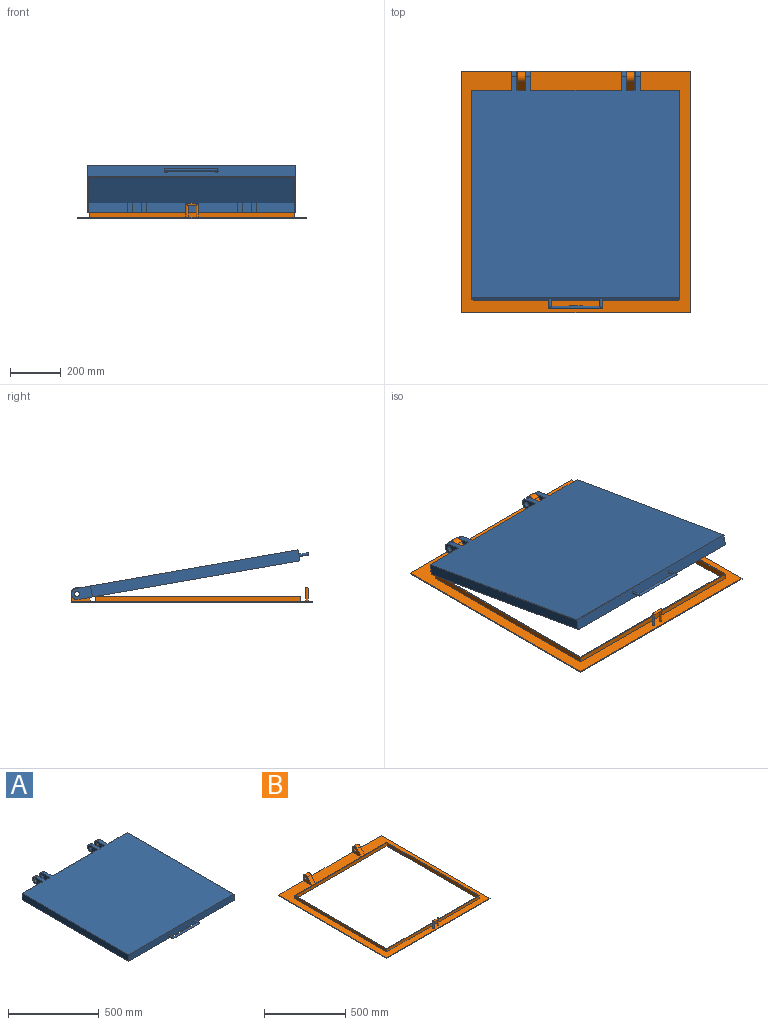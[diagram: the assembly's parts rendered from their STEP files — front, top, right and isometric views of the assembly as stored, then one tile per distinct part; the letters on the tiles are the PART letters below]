
ASSEMBLY  parts=2 mates=1
PART A: 38 faces, bbox 820x950x44 mm
  f0: plane 160x44mm, normal (0,1,0), area 7040mm2, adj f6,f8,f13,f25
  f1: plane 44x35mm, normal (0,1,0), area 1540mm2, adj f8,f13,f22,f24
  f2: plane 355x44mm, normal (0,1,0), area 15620mm2, adj f8,f13,f19,f23
  f3: plane 44x35mm, normal (0,1,0), area 1540mm2, adj f8,f13,f18,f21
  f4: plane 820x44mm, normal (0,-1,0), area 35922.9mm2, adj f6,f7,f8,f13,f15,f17
  f5: plane 155x44mm, normal (0,1,0), area 6820mm2, adj f7,f8,f13,f20
  f6: plane 830x44mm, normal (-1,0,0), area 36520mm2, adj f0,f4,f8,f13
  f7: plane 830x44mm, normal (1,0,0), area 36520mm2, adj f4,f5,f8,f13
  f8: plane 887.5x820mm, normal (0,0,1), area 685200mm2, adj f0,f1,f2,f3,f4,f5,f6,f7
  f9: plane 822x40mm, normal (-1,0,0), area 32880mm2, adj f10,f12,f13,f14
  f10: plane 812x40mm, normal (0,-1,0), area 32480mm2, adj f9,f11,f13,f14
  f11: plane 822x40mm, normal (1,0,0), area 32880mm2, adj f10,f12,f13,f14
  f12: plane 812x40mm, normal (0,1,0), area 32480mm2, adj f9,f11,f13,f14
  f13: plane 887.5x820mm, normal (0,0,-1), area 17736mm2, adj f0,f1,f2,f3,f4,f5,f6,f7
  f14: plane 822x812mm, normal (0,0,-1), area 667464mm2, adj f9,f10,f11,f12
  f15: cylinder r=5mm len=40mm, axis (0,1,0), area 1099.6mm2, adj f4,f16
  f16: cylinder r=5mm len=210mm, axis (1,0,0), area 6277.8mm2, adj f15,f17
  f17: cylinder r=5mm len=40mm, axis (0,-1,0), area 1094.2mm2, adj f4,f16
  f18: plane 79.99x44mm, normal (1,0,0), area 2988.6mm2, adj f3,f8,f13,f32,f33,f37
  f19: plane 79.99x44mm, normal (-1,0,0), area 2988.6mm2, adj f2,f8,f13,f32,f33,f37
  f20: plane 79.99x44mm, normal (1,0,0), area 2988.6mm2, adj f5,f8,f13,f30,f31,f36
  f21: plane 79.99x44mm, normal (-1,0,0), area 2988.6mm2, adj f3,f8,f13,f30,f31,f36
  f22: plane 79.99x44mm, normal (-1,0,0), area 2988.6mm2, adj f1,f8,f13,f28,f29,f35
  f23: plane 79.99x44mm, normal (1,0,0), area 2988.6mm2, adj f2,f8,f13,f28,f29,f35
  f24: plane 79.99x44mm, normal (1,0,0), area 2988.6mm2, adj f1,f8,f13,f26,f27,f34
  f25: plane 79.99x44mm, normal (-1,0,0), area 2988.6mm2, adj f0,f8,f13,f26,f27,f34
  f26: cylinder r=22.5mm len=22.49mm, axis (1,0,0), area 696.9mm2, adj f8,f24,f25,f27
  f27: cylinder r=22.5mm len=22.49mm, axis (1,0,0), area 696.9mm2, adj f13,f24,f25,f26
  f28: cylinder r=22.5mm len=22.49mm, axis (1,0,0), area 696.9mm2, adj f13,f22,f23,f29
  f29: cylinder r=22.5mm len=22.49mm, axis (1,0,0), area 696.9mm2, adj f8,f22,f23,f28
  f30: cylinder r=22.5mm len=22.49mm, axis (1,0,0), area 696.9mm2, adj f8,f20,f21,f31
  f31: cylinder r=22.5mm len=22.49mm, axis (1,0,0), area 696.9mm2, adj f13,f20,f21,f30
  f32: cylinder r=22.5mm len=22.49mm, axis (1,0,0), area 696.9mm2, adj f8,f18,f19,f33
  f33: cylinder r=22.5mm len=22.49mm, axis (1,0,0), area 696.9mm2, adj f13,f18,f19,f32
  f34: cylinder r=10mm len=20mm, axis (-1,0,0), area 1256.6mm2, adj f24,f25
  f35: cylinder r=10mm len=20mm, axis (-1,0,0), area 1256.6mm2, adj f22,f23
  f36: cylinder r=10mm len=20mm, axis (-1,0,0), area 1256.6mm2, adj f20,f21
  f37: cylinder r=10mm len=20mm, axis (-1,0,0), area 1256.6mm2, adj f18,f19
PART B: 28 faces, bbox 900x950x59 mm
  f0: plane 950x900mm, normal (0,0,1), area 197379mm2, adj f1,f2,f7,f9,f10,f11,f12,f14
  f1: plane 950x4mm, normal (1,0,0), area 3800mm2, adj f0,f7,f8,f14
  f2: plane 950x4mm, normal (-1,0,0), area 3800mm2, adj f0,f7,f8,f14
  f3: plane 800x24mm, normal (1,0,0), area 19200mm2, adj f4,f6,f8,f13
  f4: plane 800x24mm, normal (0,-1,0), area 19200mm2, adj f3,f5,f8,f13
  f5: plane 800x24mm, normal (-1,0,0), area 19200mm2, adj f4,f6,f8,f13
  f6: plane 800x24mm, normal (0,1,0), area 19200mm2, adj f3,f5,f8,f13
  f7: plane 900x4mm, normal (0,-1,0), area 3600mm2, adj f0,f1,f2,f8
  f8: plane 950x900mm, normal (0,0,-1), area 215000mm2, adj f1,f2,f3,f4,f5,f6,f7,f14
  f9: plane 808x20mm, normal (1,0,0), area 16160mm2, adj f0,f10,f12,f13
  f10: plane 808x20mm, normal (0,1,0), area 16160mm2, adj f0,f9,f11,f13
  f11: plane 808x20mm, normal (-1,0,0), area 16160mm2, adj f0,f10,f12,f13
  f12: plane 808x20mm, normal (0,-1,0), area 16160mm2, adj f0,f9,f11,f13
  f13: plane 808x808mm, normal (0,0,1), area 12864mm2, adj f3,f4,f5,f6,f9,f10,f11,f12
  f14: plane 900x36.12mm, normal (0,1,0), area 5527.4mm2, adj f0,f1,f2,f8,f15,f17,f18,f21
  f15: cylinder r=21.67mm len=38.31mm, axis (-1,0,0), area 1590.6mm2, adj f14,f16,f17,f18
  f16: plane 46x38.35mm, normal (0,-0.77,0.64), area 1796.7mm2, adj f0,f15,f17,f18
  f17: plane 76.67x53.79mm, normal (1,0,0), area 2488.7mm2, adj f0,f14,f15,f16,f19
  f18: plane 76.67x53.79mm, normal (-1,0,0), area 2488.7mm2, adj f0,f14,f15,f16,f19
  f19: cylinder r=10mm len=30mm, axis (-1,0,0), area 1885mm2, adj f17,f18
  f20: plane 46x38.35mm, normal (0,-0.77,0.64), area 1796.7mm2, adj f0,f21,f22,f23
  f21: cylinder r=21.67mm len=38.31mm, axis (1,0,0), area 1590.6mm2, adj f14,f20,f22,f23
  f22: plane 76.67x53.79mm, normal (-1,0,0), area 2488.7mm2, adj f0,f14,f20,f21,f24
  f23: plane 76.67x53.79mm, normal (1,0,0), area 2488.7mm2, adj f0,f14,f20,f21,f24
  f24: cylinder r=10mm len=30mm, axis (1,0,0), area 1885mm2, adj f22,f23
  f25: cylinder r=5mm len=55mm, axis (0,0,-1), area 1570.8mm2, adj f0,f26
  f26: cylinder r=5mm len=50mm, axis (1,0,0), area 1256.6mm2, adj f25,f27
  f27: cylinder r=5mm len=55mm, axis (0,0,1), area 1570.8mm2, adj f0,f26
PLACE A rot(axis=(-1,0,0),9.9deg) t=(-1.59,38.42,108.63)mm
PLACE B t=(0.91,27.36,-22.89)mm fixed
MATE revolute A.f26 <-> B.f19  axis (-1,0,0) through (-251.59,505.69,8.61)mm
